# Revit family: 305_A56_
name_source: partatom
category: Pipe Accessories
revit_build: Autodesk Revit 2018 (Build: 20170223_1515(x64)
units: mm (PartAtom-declared; Revit-internal decimal feet)

## family parameters
Always vertical = Yes
Cut with Voids When Loaded = No
Part Type = Valve - Breaks Into
Round Connector Dimension = Use Diameter
Shared = No
Work Plane-Based = No

## types (2) — shared parameters
CAT0 = Yes
Description = MALE THREAD ANGLE HOSE VALVE
HH = 25 mm  [stored 0.082021 ft]
HH__ve = -25 mm  [stored -0.082021 ft]
L2D_Min = 3048 mm  [stored 10 ft]
Manufacturer = Giacomini
QmdConnectorList = 301;D;302;D
R1 = 20 mm  [stored 0.0656168 ft]
R12 = 10 mm  [stored 0.0328084 ft]
URL = http://www.giacomini.com
magiPartTypeId = 305
magiProductFamilyId = A56*
zero-valued in all types: MC_Default_elevation

## per-type parameters (varying)
| type | A2 | BH | D | HB | HN | HP | HP__ve | HT | L | L2D | RB | RN | RP | TH | W2D |
| A56Y001 | 51 mm  [stored 0.167323 ft] | 47 mm  [stored 0.154199 ft] | 40 mm | 60 mm  [stored 0.19685 ft] | 23 mm  [stored 0.0754593 ft] | 23 mm  [stored 0.0754593 ft] | -23 mm | 146 mm | 57 mm | 57 mm | 40 mm  [stored 0.131234 ft] | 34 mm | 24 mm  [stored 0.0787402 ft] | 75 mm | 40 mm  [stored 0.131234 ft] |
| A56Y005 | 65 mm  [stored 0.213255 ft] | 67 mm  [stored 0.219816 ft] | 65 mm | 98 mm | 28 mm  [stored 0.0918635 ft] | 31 mm  [stored 0.101706 ft] | -31 mm  [stored -0.101706 ft] | 202 mm | 81 mm  [stored 0.265748 ft] | 81 mm  [stored 0.265748 ft] | 56 mm  [stored 0.183727 ft] | 48 mm  [stored 0.15748 ft] | 39 mm  [stored 0.127953 ft] | 109 mm | 65 mm  [stored 0.213255 ft] |

note: column(s) folded — value = type name in every type: magiProductCode, magiProductId

note: [stored X ft] marks values corroborated as IEEE doubles in the binary element streams (Revit-internal decimal feet)

## geometry (parser evidence)
native form markers: Sweep x3
no freeform markers — native parametric forms only
